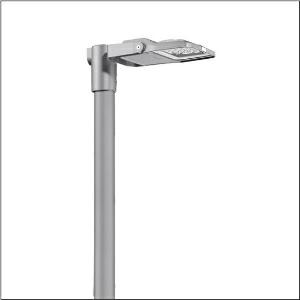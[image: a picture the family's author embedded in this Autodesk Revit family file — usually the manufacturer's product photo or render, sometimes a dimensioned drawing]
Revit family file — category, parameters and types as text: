
# Revit family: floodlight_fl_21_iq_micro___pl64_5xa7761a4e3a_8e2d
name_source: partatom
category: Lighting Fixtures
units: mm (PartAtom-declared; Revit-internal decimal feet)

## family parameters
Cut with Voids When Loaded = No
Host = Face
Light Source = No
Part Type = Normal
Room Calculation Point = No
Round Connector Dimension = Use Diameter
Shared = No

## types (1)
- --- (1 x LED, 2980 lm, 23.1 W, 4000K)
    Apparent Load = 23 VA
    CIE Flux Codes = 28 80 98 100 100
    Color Rendering = 70
    Color Temperature = 4000K
    Default Elevation = 1800 mm
    Description = Floodlight FL 21 iQ micro, floodlight, primary light control with lens, of PMMA, primary optical cover: protective disc, of toughened safety glass, transparent, light distribution: PL64, light emission: direct distribution, installation type: surface-mounted, LED, High Power LED, rated luminous flux: 2.980lm, luminous efficacy: 129lm/W, light colour: 740, colour temperature: 4000K, control: optimised constant luminous flux control (CLO 2.0), Desk-Remote (wireless, voltage-free reading and setting of iQ features in the workshop via application-optimized NFC function/RFID function), Light-Fading, Smart-Wire, Night-Set, Lumen-Switch, Temp-Guard, Auto-Match, with terminal, 6-pole, mains connection: 220..240V, AC, 50/60Hz, start of lifetime: 23W, end of service life: 24W, reduction: 11W, luminaire housing, of diecast aluminium, powder-coated, Siteco® metallic grey (DB 702S), corrosivity category C5 mid according to DIN EN ISO 12944, sealing non-destructively replaceable, please order mast flange separately, mast bracket, of steel, galvanised, powder-coated, Siteco® metallic grey (DB 702S), protection rating (complete): IP66, insulation class (complete): insulation class II (safety insulation), certification: CE, ENEC, VDE, protection symbol: D, impact resistance: IK07, permissible operating ambient temperature: -40..+40°C, permissible operating ambient temperature for outdoor applications: -40..+50°C, standard: DIN EN 12944, LABS conformity tested according to VDMA 24364:2018-05, packaging unit: 1 piece

Light Distribution: PL64
    Height = 65 mm
    Lamp = 1 x LED
    Lamp Light Flux = 2980 lm
    Lamp Power = 23.1 W
    Lamp count = 1
    Length = 312 mm
    Luminous efficacy = 129 lm/W
    Manufacturer = Siteco
    ModVariant = No
    Model = 5XA7761A4E3A
    Number of Poles = 1
    OnlyDefault = Yes
    Power Factor = 1
    Product Name = Floodlight FL 21 iQ micro | PL64
    Product group = floodlight | pylon annexe
    ProductGroupID = 6200
    Protection Class = Protection class II
    Protection Degree = IP 66
    RLX_Detail_Level = 1
    RLX_Emergency_Light_Flux = 0 lm
    RLX_Emergency_Type = 0
    RLX_Emergency_Type_DB = No
    RlxData = <blob elided: 101841 chars, md5=4bf920f7>
    Socket = socket
    Standby Power = 0 W
    System Light Flux = 2980 lm
    System Power = 23 W
    Type Comments = factory setting: luminous flux: 100 % | dim-lin: 254 | 455 mA
    Type Image = l_1007121.jpg
    URL = http://relux.com
    VarID = @adj_132159
    Voltage = 0 V
    Weight = 0.00 kg
    Width = 230 mm

## geometry (parser evidence)
native form markers: Blend x4, Sweep x11
no freeform markers — native parametric forms only
